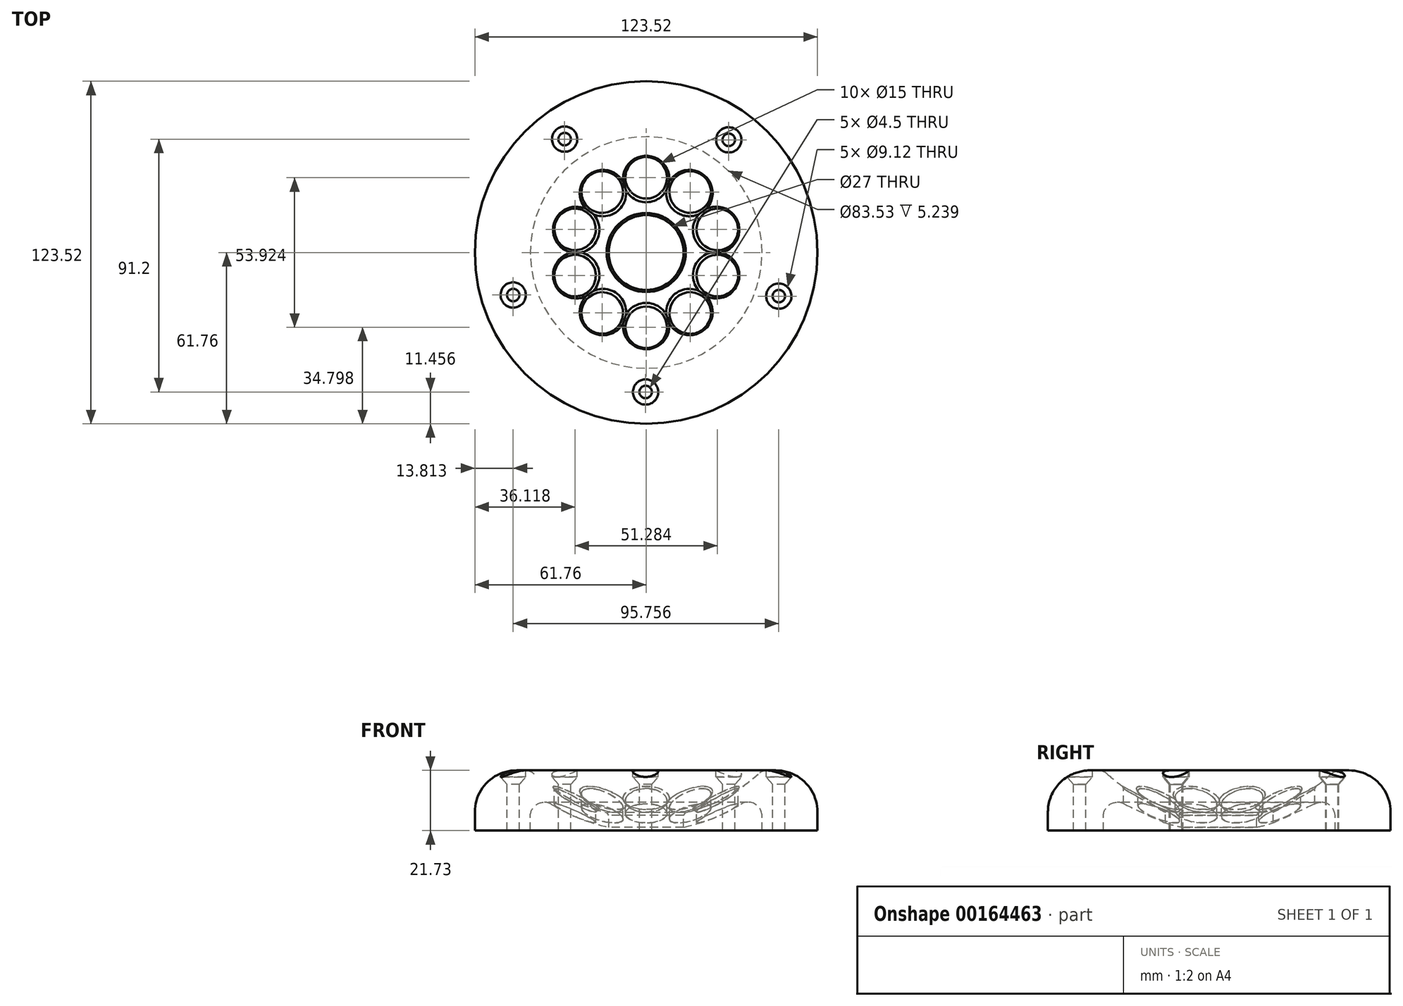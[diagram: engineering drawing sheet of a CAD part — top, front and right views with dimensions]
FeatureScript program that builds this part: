
annotation { "Feature Type Name" : "Feature", "Feature Type Description" : "" }
export const myFeature = defineFeature(function(context is Context, id is Id, definition is map)
    precondition{}
    {
        {
            var Q0;
            Q0=qCreatedBy(makeId("Front.planeOp"),FACE);
            var sketch = newSketch(context, id + "F0", { "sketchPlane" : qUnion([Q0])});
            skLineSegment(sketch, "E0", {"start": v(0, 187.8) * mm, "end": v(0, -191.67) * mm, "construction": true});
            skArc(sketch, "E1", {"start": v(13.5, 6.35) * mm, "mid": v(27.84, 11.66) * mm, "end": v(40.38, 20.43) * mm});
            skArc(sketch, "E2.1", {"start": v(13.5, 1.22) * mm, "mid": v(24.18, 4.47) * mm, "end": v(34.14, 9.5) * mm});
            skLineSegment(sketch, "E3.left", {"start": v(13.5, 1.22) * mm, "end": v(13.5, 6.35) * mm});
            skLineSegment(sketch, "E4.bottom", {"start": v(41.76, 0) * mm, "end": v(61.76, 0) * mm});
            skLineSegment(sketch, "E4.left", {"start": v(41.76, 0) * mm, "end": v(41.76, 5.24) * mm});
            skLineSegment(sketch, "E4.right", {"start": v(61.76, 0) * mm, "end": v(61.76, 6.73) * mm});
            skLineSegment(sketch, "E5", {"start": v(43.74, 21.73) * mm, "end": v(46.76, 21.73) * mm});
            skPoint(sketch, "E6.visualSharp", {"position": v(61.76, 21.73) * mm});
            skArc(sketch, "E6.filletArc", {"start": v(61.76, 6.73) * mm, "mid": v(57.37, 17.34) * mm, "end": v(46.76, 21.73) * mm});
            skPoint(sketch, "E7.visualSharp", {"position": v(41.76, 21.73) * mm});
            skArc(sketch, "E7.filletArc", {"start": v(43.74, 21.73) * mm, "mid": v(41.94, 21.4) * mm, "end": v(40.38, 20.43) * mm});
            skPoint(sketch, "E8.visualSharp", {"position": v(41.76, 15) * mm});
            skArc(sketch, "E8.filletArc", {"start": v(41.76, 5.24) * mm, "mid": v(39.2, 9.6) * mm, "end": v(34.14, 9.5) * mm});
            skSolve(sketch);
        }
        {
            var Q0;
            Q0=makeQuery(id+"F0.imprint","IMPRINT",FACE,{"disambiguationData":[TD([[makeQuery(id+"F0.imprint","IMPRINT",EDGE,{"derivedFrom":sQuery(id+"F0.wireOp",EDGE,"E1")}),-1.0]])]});
            var Q1;
            Q1=sQuery(id+"F0.wireOp",EDGE,"E0");
            revolve(context, id + "F1", {"entities" : qUnion([Q0]), "axis" : qUnion([Q1]), "revolveType" : RevolveType.FULL});
        }
        {
            var Q0;
            Q0=makeQuery(id+"F1.opRevolve","SWEPT_FACE",FACE,{"disambiguationData":[OSD([sQuery(id+"F0.wireOp",EDGE,"E5")])]});
            var sketch = newSketch(context, id + "F2", { "sketchPlane" : qUnion([Q0])});
            skCircle(sketch, "E9", {"center": v(0, 0) * mm, "radius": 50.3 * mm, "construction": true});
            skPoint(sketch, "E10", {"position": v(-0.22, -50.3) * mm});
            skPoint(sketch, "E11.1.0", {"position": v(47.8, -15.73) * mm});
            skPoint(sketch, "E11.2.0", {"position": v(29.77, 40.63) * mm});
            skPoint(sketch, "E11.3.0", {"position": v(-29.4, 40.9) * mm});
            skPoint(sketch, "E11.4.0", {"position": v(-47.95, -15.3) * mm});
            skPoint(sketch, "E11.center", {"position": v(0, 0.04) * mm});
            skCircle(sketch, "E12", {"center": v(0, -26.96) * mm, "radius": 7.5 * mm});
            skCircle(sketch, "E13.1.0", {"center": v(15.85, -21.81) * mm, "radius": 7.5 * mm});
            skCircle(sketch, "E13.2.0", {"center": v(25.64, -8.33) * mm, "radius": 7.5 * mm});
            skCircle(sketch, "E13.3.0", {"center": v(25.64, 8.33) * mm, "radius": 7.5 * mm});
            skCircle(sketch, "E13.4.0", {"center": v(15.85, 21.81) * mm, "radius": 7.5 * mm});
            skCircle(sketch, "E13.5.0", {"center": v(0, 26.96) * mm, "radius": 7.5 * mm});
            skCircle(sketch, "E13.6.0", {"center": v(-15.85, 21.81) * mm, "radius": 7.5 * mm});
            skCircle(sketch, "E13.7.0", {"center": v(-25.64, 8.33) * mm, "radius": 7.5 * mm});
            skCircle(sketch, "E13.8.0", {"center": v(-25.64, -8.33) * mm, "radius": 7.5 * mm});
            skCircle(sketch, "E13.9.0", {"center": v(-15.85, -21.81) * mm, "radius": 7.5 * mm});
            skSolve(sketch);
        }
        {
            var Q0;
            Q0=sQuery(id+"F2.wireOp",VERTEX,"E10");
            var Q1;
            Q1=sQuery(id+"F2.wireOp",VERTEX,"E11.1.0");
            var Q2;
            Q2=sQuery(id+"F2.wireOp",VERTEX,"E11.2.0");
            var Q3;
            Q3=sQuery(id+"F2.wireOp",VERTEX,"E11.3.0");
            var Q4;
            Q4=sQuery(id+"F2.wireOp",VERTEX,"E11.4.0");
            var Q5;
            Q5=makeQuery(id+"F1.opRevolve","SWEPT_BODY",BODY,{"disambiguationData":[OSD([sQuery(id+"F0.wireOp",EDGE,"E1"),sQuery(id+"F0.wireOp",EDGE,"E2.1"),sQuery(id+"F0.wireOp",EDGE,"E3.left"),sQuery(id+"F0.wireOp",EDGE,"E4.bottom"),sQuery(id+"F0.wireOp",EDGE,"E4.left"),sQuery(id+"F0.wireOp",EDGE,"E4.right"),sQuery(id+"F0.wireOp",EDGE,"E5"),sQuery(id+"F0.wireOp",EDGE,"E6.filletArc"),sQuery(id+"F0.wireOp",EDGE,"E7.filletArc"),sQuery(id+"F0.wireOp",EDGE,"E8.filletArc")])]});
            hole(context, id + "F3", {"style" : HoleStyle.C_SINK, "endStyle" : HoleEndStyle.THROUGH, "standardTappedOrClearance" : lookupTablePath({ "standard" : "ANSI", "fit" : "Normal (ASME)", "size" : "#8", "type" : "Clearance" }), "standardBlindInLast" : lookupTablePath({ "fit" : "Free", "standard" : "ANSI", "size" : "#8", "type" : "Clearance" }), "holeDiameter" : 4.5 * mm, "cSinkDiameter" : 9.12 * mm, "cSinkAngle" : 82 * degree, "locations" : qUnion([Q0, Q1, Q2, Q3, Q4]), "scope" : qUnion([Q5]), "isTappedThrough" : true});
        }
        {
            var Q0;
            Q0=makeQuery(id+"F2.imprint","IMPRINT",FACE,{"disambiguationData":[TD([[makeQuery(id+"F2.imprint","IMPRINT",EDGE,{"derivedFrom":sQuery(id+"F2.wireOp",EDGE,"E13.6.0")}),1.0]])]});
            var Q1;
            Q1=makeQuery(id+"F2.imprint","IMPRINT",FACE,{"disambiguationData":[TD([[makeQuery(id+"F2.imprint","IMPRINT",EDGE,{"derivedFrom":sQuery(id+"F2.wireOp",EDGE,"E13.5.0")}),1.0]])]});
            var Q2;
            Q2=makeQuery(id+"F2.imprint","IMPRINT",FACE,{"disambiguationData":[TD([[makeQuery(id+"F2.imprint","IMPRINT",EDGE,{"derivedFrom":sQuery(id+"F2.wireOp",EDGE,"E13.4.0")}),1.0]])]});
            var Q3;
            Q3=makeQuery(id+"F2.imprint","IMPRINT",FACE,{"disambiguationData":[TD([[makeQuery(id+"F2.imprint","IMPRINT",EDGE,{"derivedFrom":sQuery(id+"F2.wireOp",EDGE,"E13.3.0")}),1.0]])]});
            var Q4;
            Q4=makeQuery(id+"F2.imprint","IMPRINT",FACE,{"disambiguationData":[TD([[makeQuery(id+"F2.imprint","IMPRINT",EDGE,{"derivedFrom":sQuery(id+"F2.wireOp",EDGE,"E13.2.0")}),1.0]])]});
            var Q5;
            Q5=makeQuery(id+"F2.imprint","IMPRINT",FACE,{"disambiguationData":[TD([[makeQuery(id+"F2.imprint","IMPRINT",EDGE,{"derivedFrom":sQuery(id+"F2.wireOp",EDGE,"E13.1.0")}),1.0]])]});
            var Q6;
            Q6=makeQuery(id+"F2.imprint","IMPRINT",FACE,{"disambiguationData":[TD([[makeQuery(id+"F2.imprint","IMPRINT",EDGE,{"derivedFrom":sQuery(id+"F2.wireOp",EDGE,"E12")}),1.0]])]});
            var Q7;
            Q7=makeQuery(id+"F2.imprint","IMPRINT",FACE,{"disambiguationData":[TD([[makeQuery(id+"F2.imprint","IMPRINT",EDGE,{"derivedFrom":sQuery(id+"F2.wireOp",EDGE,"E13.9.0")}),1.0]])]});
            var Q8;
            Q8=makeQuery(id+"F2.imprint","IMPRINT",FACE,{"disambiguationData":[TD([[makeQuery(id+"F2.imprint","IMPRINT",EDGE,{"derivedFrom":sQuery(id+"F2.wireOp",EDGE,"E13.8.0")}),1.0]])]});
            var Q9;
            Q9=makeQuery(id+"F2.imprint","IMPRINT",FACE,{"disambiguationData":[TD([[makeQuery(id+"F2.imprint","IMPRINT",EDGE,{"derivedFrom":sQuery(id+"F2.wireOp",EDGE,"E13.7.0")}),1.0]])]});
            extrude(context, id + "F4", {"entities" : qUnion([Q0, Q1, Q2, Q3, Q4, Q5, Q6, Q7, Q8, Q9]), "operationType" : NewBodyOperationType.REMOVE, "endBound" : BoundingType.THROUGH_ALL, "oppositeDirection" : true, "depth" : 25 * mm});
        }
        {
            var Q0;
            Q0=makeQuery(id+"F1.opRevolve","SWEPT_EDGE",EDGE,{"disambiguationData":[OSD([sQuery(id+"F0.wireOp",EDGE,"E1"),sQuery(id+"F0.wireOp",EDGE,"E3.left")])]});
            var Q1;
            Q1=makeQuery(id+"F4.boolean.opBoolean","INTERSECT",EDGE,{"derivedFrom":[makeQuery(id+"F1.opRevolve","SWEPT_FACE",FACE,{"disambiguationData":[OSD([sQuery(id+"F0.wireOp",EDGE,"E1")])]}),makeQuery(id+"F4.opExtrude","SWEPT_FACE",FACE,{"disambiguationData":[OSD([sQuery(id+"F2.wireOp",EDGE,"E13.6.0")])]})]});
            var Q2;
            Q2=makeQuery(id+"F4.boolean.opBoolean","INTERSECT",EDGE,{"derivedFrom":[makeQuery(id+"F1.opRevolve","SWEPT_FACE",FACE,{"disambiguationData":[OSD([sQuery(id+"F0.wireOp",EDGE,"E1")])]}),makeQuery(id+"F4.opExtrude","SWEPT_FACE",FACE,{"disambiguationData":[OSD([sQuery(id+"F2.wireOp",EDGE,"E13.5.0")])]})]});
            var Q3;
            Q3=makeQuery(id+"F4.boolean.opBoolean","INTERSECT",EDGE,{"derivedFrom":[makeQuery(id+"F1.opRevolve","SWEPT_FACE",FACE,{"disambiguationData":[OSD([sQuery(id+"F0.wireOp",EDGE,"E1")])]}),makeQuery(id+"F4.opExtrude","SWEPT_FACE",FACE,{"disambiguationData":[OSD([sQuery(id+"F2.wireOp",EDGE,"E13.4.0")])]})]});
            var Q4;
            Q4=makeQuery(id+"F4.boolean.opBoolean","INTERSECT",EDGE,{"derivedFrom":[makeQuery(id+"F1.opRevolve","SWEPT_FACE",FACE,{"disambiguationData":[OSD([sQuery(id+"F0.wireOp",EDGE,"E1")])]}),makeQuery(id+"F4.opExtrude","SWEPT_FACE",FACE,{"disambiguationData":[OSD([sQuery(id+"F2.wireOp",EDGE,"E13.3.0")])]})]});
            var Q5;
            Q5=makeQuery(id+"F4.boolean.opBoolean","INTERSECT",EDGE,{"derivedFrom":[makeQuery(id+"F1.opRevolve","SWEPT_FACE",FACE,{"disambiguationData":[OSD([sQuery(id+"F0.wireOp",EDGE,"E1")])]}),makeQuery(id+"F4.opExtrude","SWEPT_FACE",FACE,{"disambiguationData":[OSD([sQuery(id+"F2.wireOp",EDGE,"E13.2.0")])]})]});
            var Q6;
            Q6=makeQuery(id+"F4.boolean.opBoolean","INTERSECT",EDGE,{"derivedFrom":[makeQuery(id+"F1.opRevolve","SWEPT_FACE",FACE,{"disambiguationData":[OSD([sQuery(id+"F0.wireOp",EDGE,"E1")])]}),makeQuery(id+"F4.opExtrude","SWEPT_FACE",FACE,{"disambiguationData":[OSD([sQuery(id+"F2.wireOp",EDGE,"E13.1.0")])]})]});
            var Q7;
            Q7=makeQuery(id+"F4.boolean.opBoolean","INTERSECT",EDGE,{"derivedFrom":[makeQuery(id+"F1.opRevolve","SWEPT_FACE",FACE,{"disambiguationData":[OSD([sQuery(id+"F0.wireOp",EDGE,"E1")])]}),makeQuery(id+"F4.opExtrude","SWEPT_FACE",FACE,{"disambiguationData":[OSD([sQuery(id+"F2.wireOp",EDGE,"E12")])]})]});
            var Q8;
            Q8=makeQuery(id+"F4.boolean.opBoolean","INTERSECT",EDGE,{"derivedFrom":[makeQuery(id+"F1.opRevolve","SWEPT_FACE",FACE,{"disambiguationData":[OSD([sQuery(id+"F0.wireOp",EDGE,"E1")])]}),makeQuery(id+"F4.opExtrude","SWEPT_FACE",FACE,{"disambiguationData":[OSD([sQuery(id+"F2.wireOp",EDGE,"E13.9.0")])]})]});
            var Q9;
            Q9=makeQuery(id+"F4.boolean.opBoolean","INTERSECT",EDGE,{"derivedFrom":[makeQuery(id+"F1.opRevolve","SWEPT_FACE",FACE,{"disambiguationData":[OSD([sQuery(id+"F0.wireOp",EDGE,"E1")])]}),makeQuery(id+"F4.opExtrude","SWEPT_FACE",FACE,{"disambiguationData":[OSD([sQuery(id+"F2.wireOp",EDGE,"E13.8.0")])]})]});
            var Q10;
            Q10=makeQuery(id+"F4.boolean.opBoolean","INTERSECT",EDGE,{"derivedFrom":[makeQuery(id+"F1.opRevolve","SWEPT_FACE",FACE,{"disambiguationData":[OSD([sQuery(id+"F0.wireOp",EDGE,"E1")])]}),makeQuery(id+"F4.opExtrude","SWEPT_FACE",FACE,{"disambiguationData":[OSD([sQuery(id+"F2.wireOp",EDGE,"E13.7.0")])]})]});
            chamfer(context, id + "F5", {"entities" : qUnion([Q0, Q1, Q2, Q3, Q4, Q5, Q6, Q7, Q8, Q9, Q10]), "width" : 1 * mm, "tangentPropagation" : true});
        }
    });
